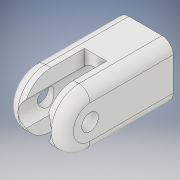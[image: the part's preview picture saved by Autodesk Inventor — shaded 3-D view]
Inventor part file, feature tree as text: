
AUTODESK INVENTOR PART (.ipt)
format: ipt  version: 2017 SP1 (Build 210196100, 196)  size: 197,120 bytes
history: native  units: in
note: dims shown in document units (in); Inventor stores cm internally (conversion verified against a paired STEP export)
features: extrude x6, sketch x6, fillet x1, plane x1, projected_geometry x1
ambient origin geometry x8: Origin, YZ Plane, XZ Plane, XY Plane, X Axis, Y Axis, Z Axis, Center Point
bodies: Solid1 (feature_tree)
feature tree (15):
  extrude  "Extrusion1"  Depth=0.3937in
  extrude  "Extrusion2"  Depth=0.3937in
  extrude  "Extrusion3"  Depth=0.1181in
  fillet  "Fillet1"  Radius=0.1181in
  extrude  "Extrusion4"  Depth=0.1181in
  plane  "Work Plane1"
  extrude  "Extrusion5"  Depth=0.1181in TaperAngle=0.0deg
  extrude  "Extrusion6"  Depth=0.0394in
  sketch  "Sketch1"  dims[d0=0.3937in d1=0.3937in]
  sketch  "Sketch2"  dims[d2=0.3543in d3=0.0in d4=0.3937in]
  sketch  "Sketch3"  dims[d5=0.5906in d6=0.1181in d7=0.1181in d8=0.0in]
  projected_geometry  "Projected Loop1"
  sketch  "Sketch4"  dims[d9=0.1181in d10=0.0in d11=0.0787in]
  sketch  "Sketch5"  dims[d12=0.1181in d13=0.1181in d14=0.0in]
  sketch  "Sketch8"  dims[d15=-0.1181in d16=0.2362in d17=0.1181in d18=0.0in d20=0.2362in d21=0.0394in d22=0.0in]
